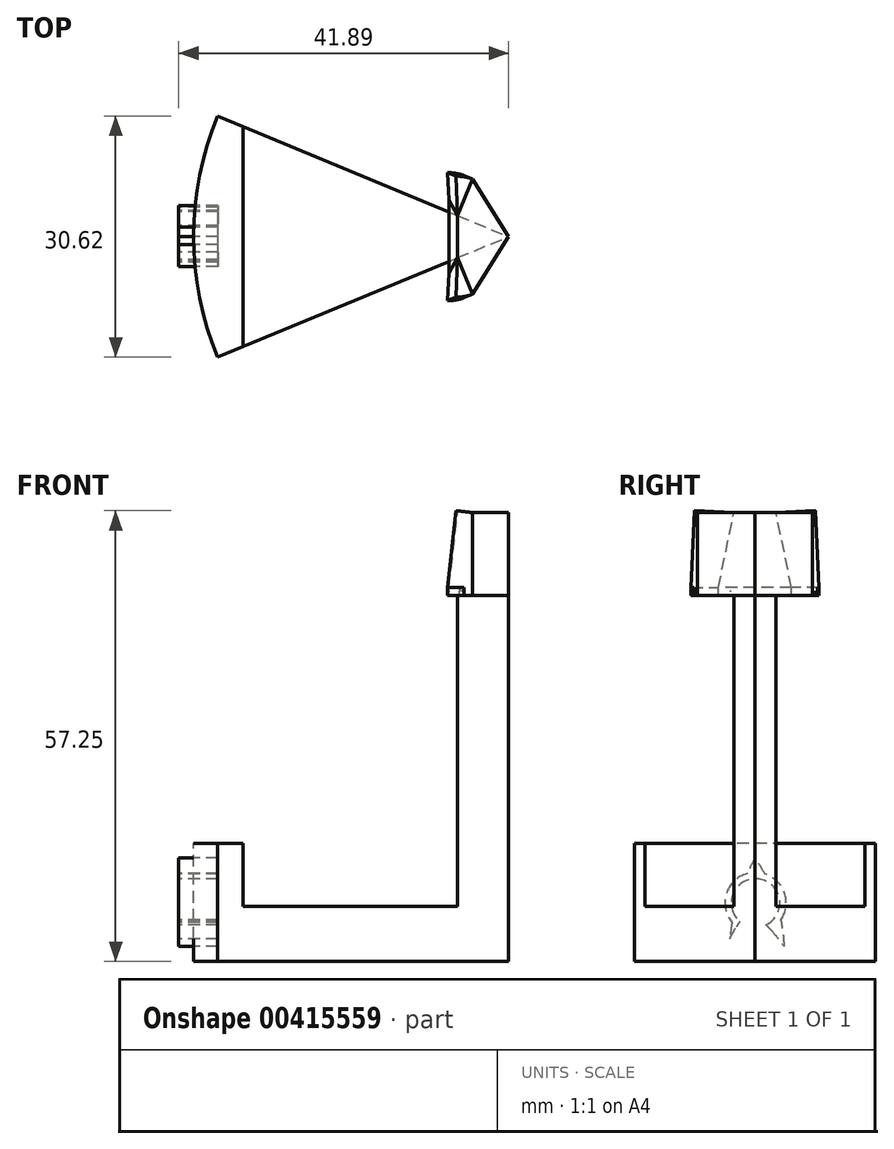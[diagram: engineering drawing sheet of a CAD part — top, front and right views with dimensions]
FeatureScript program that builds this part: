
annotation { "Feature Type Name" : "Feature", "Feature Type Description" : "" }
export const myFeature = defineFeature(function(context is Context, id is Id, definition is map)
    precondition{}
    {
        {
            var Q0;
            Q0=qCreatedBy(makeId("Front.planeOp"),FACE);
            var sketch = newSketch(context, id + "F0", { "sketchPlane" : qUnion([Q0])});
            skLineSegment(sketch, "E0", {"start": v(-37.1, 26.7) * mm, "end": v(-30.1, 26.7) * mm});
            skLineSegment(sketch, "E1", {"start": v(-30.1, 26.7) * mm, "end": v(-30.1, -30.3) * mm});
            skLineSegment(sketch, "E2", {"start": v(-30.1, -30.3) * mm, "end": v(-70.1, -30.3) * mm});
            skLineSegment(sketch, "E3", {"start": v(-70.1, -30.3) * mm, "end": v(-70.1, -15.3) * mm});
            skLineSegment(sketch, "E4", {"start": v(-70.1, -15.3) * mm, "end": v(-63.1, -15.3) * mm});
            skLineSegment(sketch, "E5", {"start": v(-63.1, -15.3) * mm, "end": v(-63.1, -23.3) * mm});
            skLineSegment(sketch, "E6", {"start": v(-63.1, -23.3) * mm, "end": v(-43.1, -23.3) * mm});
            skLineSegment(sketch, "E7", {"start": v(-37.1, 26.7) * mm, "end": v(-43.1, -23.3) * mm});
            skSolve(sketch);
        }
        {
            var Q0;
            Q0=makeQuery(id+"F0.imprint","IMPRINT",FACE,{"disambiguationData":[TD([[makeQuery(id+"F0.imprint","IMPRINT",EDGE,{"derivedFrom":sQuery(id+"F0.wireOp",EDGE,"E0")}),-1.0]])]});
            var Q1;
            Q1=sQuery(id+"F0.wireOp",EDGE,"E1");
            revolve(context, id + "F1", {"entities" : qUnion([Q0]), "axis" : qUnion([Q1]), "revolveType" : RevolveType.SYMMETRIC, "angle" : 45 * degree});
        }
        {
            var Q0;
            Q0=makeQuery(id+"F1.opRevolve","CAP_FACE",FACE,{"disambiguationData":[OSD([sQuery(id+"F0.wireOp",EDGE,"E0"),sQuery(id+"F0.wireOp",EDGE,"E1"),sQuery(id+"F0.wireOp",EDGE,"E2"),sQuery(id+"F0.wireOp",EDGE,"E3"),sQuery(id+"F0.wireOp",EDGE,"E4"),sQuery(id+"F0.wireOp",EDGE,"E5"),sQuery(id+"F0.wireOp",EDGE,"E6"),sQuery(id+"F0.wireOp",EDGE,"E7")])],"isStart":true});
            var sketch = newSketch(context, id + "F2", { "sketchPlane" : qUnion([Q0])});
            skLineSegment(sketch, "E8", {"start": v(-34.81, 26.7) * mm, "end": v(-27.81, 26.7) * mm});
            skLineSegment(sketch, "E9", {"start": v(-27.81, 26.7) * mm, "end": v(-27.81, 16.7) * mm});
            skLineSegment(sketch, "E10", {"start": v(-27.81, 16.7) * mm, "end": v(-36.01, 16.7) * mm});
            skLineSegment(sketch, "E11", {"start": v(-36.01, 16.7) * mm, "end": v(-34.81, 26.7) * mm});
            skSolve(sketch);
        }
        {
            var Q0;
            Q0 = qSketchRegion(id + "F2", true);
            extrude(context, id + "F3", {"entities" : qUnion([Q0]), "operationType" : NewBodyOperationType.ADD, "depth" : 5 * mm});
        }
        {
            var Q0;
            Q0=makeQuery(id+"F1.opRevolve","CAP_FACE",FACE,{"disambiguationData":[OSD([sQuery(id+"F0.wireOp",EDGE,"E0"),sQuery(id+"F0.wireOp",EDGE,"E1"),sQuery(id+"F0.wireOp",EDGE,"E2"),sQuery(id+"F0.wireOp",EDGE,"E3"),sQuery(id+"F0.wireOp",EDGE,"E4"),sQuery(id+"F0.wireOp",EDGE,"E5"),sQuery(id+"F0.wireOp",EDGE,"E6"),sQuery(id+"F0.wireOp",EDGE,"E7")])],"isStart":false});
            var sketch = newSketch(context, id + "F4", { "sketchPlane" : qUnion([Q0])});
            skLineSegment(sketch, "E12", {"start": v(27.81, 26.7) * mm, "end": v(27.81, 16.7) * mm});
            skLineSegment(sketch, "E13", {"start": v(27.81, 16.7) * mm, "end": v(36.01, 16.7) * mm});
            skLineSegment(sketch, "E14", {"start": v(36.01, 16.7) * mm, "end": v(34.81, 26.7) * mm});
            skLineSegment(sketch, "E15", {"start": v(34.81, 26.7) * mm, "end": v(27.81, 26.7) * mm});
            skSolve(sketch);
        }
        {
            var Q0;
            Q0 = qSketchRegion(id + "F4", true);
            extrude(context, id + "F5", {"entities" : qUnion([Q0]), "operationType" : NewBodyOperationType.ADD, "depth" : 5 * mm});
        }
        {
            var Q0;
            Q0=makeQuery(id+"F5.boolean.opBoolean","MERGE",FACE,{"derivedFrom":[makeQuery(id+"F3.boolean.opBoolean","MERGE",FACE,{"derivedFrom":[makeQuery(id+"F1.opRevolve","SWEPT_FACE",FACE,{"disambiguationData":[OSD([sQuery(id+"F0.wireOp",EDGE,"E0")])]}),makeQuery(id+"F3.opExtrude","SWEPT_FACE",FACE,{"disambiguationData":[OSD([sQuery(id+"F2.wireOp",EDGE,"E8")])]})]}),makeQuery(id+"F5.opExtrude","SWEPT_FACE",FACE,{"disambiguationData":[OSD([sQuery(id+"F4.wireOp",EDGE,"E15")])]})]});
            var sketch = newSketch(context, id + "F6", { "sketchPlane" : qUnion([Q0])});
            skLineSegment(sketch, "E16.0", {"start": v(-34.66, 7.3) * mm, "end": v(-36.57, 2.68) * mm});
            skArc(sketch, "E16.1", {"start": v(-36.57, 2.68) * mm, "mid": v(-37.1, 0) * mm, "end": v(-36.57, -2.68) * mm});
            skLineSegment(sketch, "E16.2", {"start": v(-34.66, -7.3) * mm, "end": v(-36.57, -2.68) * mm});
            skLineSegment(sketch, "E17", {"start": v(-34.66, 7.3) * mm, "end": v(-30.1, 0) * mm});
            skLineSegment(sketch, "E18", {"start": v(-30.1, 0) * mm, "end": v(-34.66, -7.3) * mm});
            skLineSegment(sketch, "E19", {"start": v(-36.57, -2.68) * mm, "end": v(-36.57, -7.3) * mm});
            skLineSegment(sketch, "E20", {"start": v(-36.57, -7.3) * mm, "end": v(-34.66, -7.3) * mm});
            skLineSegment(sketch, "E21", {"start": v(-36.57, 2.68) * mm, "end": v(-36.57, 7.3) * mm});
            skLineSegment(sketch, "E22", {"start": v(-36.57, 7.3) * mm, "end": v(-34.66, 7.3) * mm});
            skSolve(sketch);
        }
        {
            var Q0;
            Q0=makeQuery(id+"F6.imprint","IMPRINT",FACE,{"disambiguationData":[TD([[makeQuery(id+"F6.imprint","IMPRINT",EDGE,{"derivedFrom":sQuery(id+"F6.wireOp",EDGE,"E17")}),1.0]])]});
            var Q1;
            Q1=makeQuery(id+"F6.imprint","IMPRINT",FACE,{"disambiguationData":[TD([[makeQuery(id+"F6.imprint","IMPRINT",EDGE,{"derivedFrom":sQuery(id+"F6.wireOp",EDGE,"E18")}),1.0]])]});
            extrude(context, id + "F7", {"entities" : qUnion([Q0, Q1]), "operationType" : NewBodyOperationType.REMOVE, "oppositeDirection" : true, "depth" : 25 * mm});
        }
        {
            var Q0;
            Q0=makeQuery(id+"F5.opExtrude","SWEPT_FACE",FACE,{"disambiguationData":[OSD([sQuery(id+"F4.wireOp",EDGE,"E14")])]});
            var Q1;
            Q1=makeQuery(id+"F5.boolean.opBoolean","MERGE",EDGE,{"derivedFrom":[makeQuery(id+"F1.opRevolve","CAP_EDGE",EDGE,{"disambiguationData":[OSD([sQuery(id+"F0.wireOp",EDGE,"E7")])],"isStart":false}),makeQuery(id+"F5.opExtrude","CAP_EDGE",EDGE,{"disambiguationData":[OSD([sQuery(id+"F4.wireOp",EDGE,"E14")])],"isStart":true})]});
            revolve(context, id + "F8", {"operationType" : NewBodyOperationType.ADD, "entities" : qUnion([Q0]), "axis" : qUnion([Q1]), "revolveType" : RevolveType.ONE_DIRECTION, "oppositeDirection" : true, "angle" : 25 * degree});
        }
        {
            var Q0;
            Q0=makeQuery(id+"F3.opExtrude","SWEPT_FACE",FACE,{"disambiguationData":[OSD([sQuery(id+"F2.wireOp",EDGE,"E11")])]});
            var Q1;
            Q1=makeQuery(id+"F3.boolean.opBoolean","MERGE",EDGE,{"derivedFrom":[makeQuery(id+"F1.opRevolve","CAP_EDGE",EDGE,{"disambiguationData":[OSD([sQuery(id+"F0.wireOp",EDGE,"E7")])],"isStart":true}),makeQuery(id+"F3.opExtrude","CAP_EDGE",EDGE,{"disambiguationData":[OSD([sQuery(id+"F2.wireOp",EDGE,"E11")])],"isStart":true})]});
            revolve(context, id + "F9", {"operationType" : NewBodyOperationType.ADD, "entities" : qUnion([Q0]), "axis" : qUnion([Q1]), "revolveType" : RevolveType.ONE_DIRECTION, "angle" : 25 * degree});
        }
        {
            var Q0;
            Q0=makeQuery(id+"F5.boolean.opBoolean","MERGE",FACE,{"derivedFrom":[makeQuery(id+"F3.boolean.opBoolean","MERGE",FACE,{"derivedFrom":[makeQuery(id+"F1.opRevolve","SWEPT_FACE",FACE,{"disambiguationData":[OSD([sQuery(id+"F0.wireOp",EDGE,"E0")])]}),makeQuery(id+"F3.opExtrude","SWEPT_FACE",FACE,{"disambiguationData":[OSD([sQuery(id+"F2.wireOp",EDGE,"E8")])]})]}),makeQuery(id+"F5.opExtrude","SWEPT_FACE",FACE,{"disambiguationData":[OSD([sQuery(id+"F4.wireOp",EDGE,"E15")])]})]});
            var sketch = newSketch(context, id + "F10", { "sketchPlane" : qUnion([Q0])});
            skPoint(sketch, "E23.0", {"position": v(-36.57, 2.68) * mm});
            skPoint(sketch, "E23.1", {"position": v(-36.57, -2.68) * mm});
            skLineSegment(sketch, "E24", {"start": v(-36.57, 2.68) * mm, "end": v(-36.57, -2.68) * mm});
            skArc(sketch, "E25.0", {"start": v(-36.57, 2.68) * mm, "mid": v(-37.1, 0) * mm, "end": v(-36.57, -2.68) * mm});
            skArc(sketch, "E26.0", {"start": v(-42.12, 4.97) * mm, "mid": v(-43.1, 0) * mm, "end": v(-42.12, -4.97) * mm});
            skLineSegment(sketch, "E27.0", {"start": v(-37.68, 3.14) * mm, "end": v(-42.12, 4.97) * mm});
            skLineSegment(sketch, "E27.1", {"start": v(-37.68, -3.14) * mm, "end": v(-42.12, -4.97) * mm});
            skLineSegment(sketch, "E27.2", {"start": v(-36.57, -2.68) * mm, "end": v(-37.68, -3.14) * mm});
            skLineSegment(sketch, "E27.3", {"start": v(-36.57, 2.68) * mm, "end": v(-37.68, 3.14) * mm});
            skSolve(sketch);
        }
        {
            var Q0;
            Q0=makeQuery(id+"F10.imprint","IMPRINT",FACE,{"disambiguationData":[TD([[makeQuery(id+"F10.imprint","IMPRINT",EDGE,{"derivedFrom":sQuery(id+"F10.wireOp",EDGE,"E25.0")}),-1.0]])]});
            var Q1;
            Q1=makeQuery(id+"F10.imprint","IMPRINT",FACE,{"disambiguationData":[TD([[makeQuery(id+"F10.imprint","IMPRINT",EDGE,{"derivedFrom":sQuery(id+"F10.wireOp",EDGE,"E24")}),-1.0]])]});
            var Q2;
            Q2=makeQuery(id+"F1.opRevolve","SWEPT_FACE",FACE,{"disambiguationData":[OSD([sQuery(id+"F0.wireOp",EDGE,"E6")])]});
            extrude(context, id + "F11", {"entities" : qUnion([Q0, Q1]), "operationType" : NewBodyOperationType.REMOVE, "endBound" : BoundingType.UP_TO_SURFACE, "oppositeDirection" : true, "endBoundEntityFace" : qUnion([Q2]), "depth" : 25 * mm});
        }
        {
            var Q0;
            Q0=makeQuery(id+"F11.boolean.opBoolean","COPY",FACE,{"derivedFrom":makeQuery(id+"F11.opExtrude","SWEPT_FACE",FACE,{"disambiguationData":[OSD([sQuery(id+"F10.wireOp",EDGE,"E24")])]})});
            var sketch = newSketch(context, id + "F12", { "sketchPlane" : qUnion([Q0])});
            skLineSegment(sketch, "E28", {"start": v(-2.68, 16.7) * mm, "end": v(-2.68, 26.7) * mm});
            skLineSegment(sketch, "E29", {"start": v(-2.68, 26.7) * mm, "end": v(2.68, 26.7) * mm});
            skLineSegment(sketch, "E30", {"start": v(2.68, 26.7) * mm, "end": v(2.68, 16.7) * mm});
            skLineSegment(sketch, "E31", {"start": v(2.68, 16.7) * mm, "end": v(-2.68, 16.7) * mm});
            skSolve(sketch);
        }
        {
            var Q0;
            Q0 = qSketchRegion(id + "F12", true);
            var Q1;
            Q1=sQuery(id+"F12.wireOp",EDGE,"E29");
            revolve(context, id + "F13", {"operationType" : NewBodyOperationType.ADD, "entities" : qUnion([Q0]), "axis" : qUnion([Q1]), "revolveType" : RevolveType.ONE_DIRECTION, "oppositeDirection" : true, "angle" : 6.75 * degree});
        }
        {
            var Q0;
            Q0=makeQuery(id+"F13.opRevolve","SWEPT_FACE",FACE,{"disambiguationData":[OSD([sQuery(id+"F12.wireOp",EDGE,"E28")])]});
            var Q1;
            Q1=makeQuery(id+"F13.opRevolve","SWEPT_FACE",FACE,{"disambiguationData":[OSD([sQuery(id+"F12.wireOp",EDGE,"E30")])]});
            extrude(context, id + "F14", {"entities" : qUnion([Q0, Q1]), "operationType" : NewBodyOperationType.ADD, "depth" : 2 * mm, "hasSecondDirection" : true, "secondDirectionOppositeDirection" : true, "secondDirectionDepth" : 2 * mm});
        }
        {
            var Q0;
            Q0=makeQuery(id+"F11.boolean.opBoolean","COPY",FACE,{"derivedFrom":makeQuery(id+"F11.opExtrude","SWEPT_FACE",FACE,{"disambiguationData":[OSD([sQuery(id+"F10.wireOp",EDGE,"E27.0"),sQuery(id+"F10.wireOp",EDGE,"E27.3")])]})});
            var Q1;
            {var subQ2=sQuery(id+"F4.wireOp",EDGE,"E14");var subQ3=sQuery(id+"F4.wireOp",EDGE,"E13");Q1=makeQuery(id+"F14.boolean.opBoolean","SPLIT",FACE,{"disambiguationData":[TD([makeQuery(id+"F5.opExtrude","SWEPT_FACE",FACE,{"disambiguationData":[OSD([subQ3])]})])],"derivedFrom":makeQuery(id+"F8.opRevolve","CAP_FACE",FACE,{"disambiguationData":[OSD([subQ2])],"isStart":false})});}
            extrude(context, id + "F15", {"entities" : qUnion([Q0, Q1]), "operationType" : NewBodyOperationType.REMOVE, "oppositeDirection" : true, "depth" : 25 * mm});
        }
        {
            var Q0;
            Q0=makeQuery(id+"F5.opExtrude","SWEPT_FACE",FACE,{"disambiguationData":[OSD([sQuery(id+"F4.wireOp",EDGE,"E13")])]});
            var sketch = newSketch(context, id + "F16", { "sketchPlane" : qUnion([Q0])});
            skLineSegment(sketch, "E32.2", {"start": v(-37.89, -8.13) * mm, "end": v(-37.75, -4.81) * mm});
            skEllipticalArc(sketch, "E32.3", {});
            skFitSpline(sketch, "E32.4", {"points": [v(-36.3, -7.94) * mm, v(-36.12, -7.9) * mm, v(-35.94, -7.83) * mm, v(-35.76, -7.75) * mm]});
            skLineSegment(sketch, "E32.5", {"start": v(-35.76, -7.75) * mm, "end": v(-34.66, -7.3) * mm});
            skLineSegment(sketch, "E32.7", {"start": v(-37.75, -3.17) * mm, "end": v(-37.75, -4.68) * mm});
            skLineSegment(sketch, "E33", {"start": v(-37.67, -3.14) * mm, "end": v(-37.68, -3.14) * mm});
            skPoint(sketch, "E34.orphan", {"position": v(-37.75, 4.68) * mm});
            skLineSegment(sketch, "E35", {"start": v(-37.75, -4.68) * mm, "end": v(-37.75, -4.81) * mm});
            skPoint(sketch, "E36.orphan", {"position": v(-37.74, -4.68) * mm});
            skLineSegment(sketch, "E37.0", {"start": v(-37.75, 4.68) * mm, "end": v(-37.75, -4.68) * mm});
            skLineSegment(sketch, "E37.1", {"start": v(-36.57, 2.68) * mm, "end": v(-36.57, -2.68) * mm});
            skLineSegment(sketch, "E38.0", {"start": v(-37.89, 8.13) * mm, "end": v(-37.75, 4.78) * mm});
            skEllipticalArc(sketch, "E38.1", {});
            skLineSegment(sketch, "E38.2", {"start": v(-34.66, 7.3) * mm, "end": v(-35.77, 7.76) * mm});
            skLineSegment(sketch, "E38.3", {"start": v(-34.66, 7.3) * mm, "end": v(-30.1, 0) * mm});
            skLineSegment(sketch, "E39", {"start": v(-37.75, 4.68) * mm, "end": v(-37.75, 4.78) * mm});
            skPoint(sketch, "E40.orphan", {"position": v(-37.74, 4.68) * mm});
            skLineSegment(sketch, "E41.0", {"start": v(-30.1, 0) * mm, "end": v(-36.57, 2.68) * mm});
            skLineSegment(sketch, "E42", {"start": v(-34.66, -7.3) * mm, "end": v(-30.1, 0) * mm});
            skLineSegment(sketch, "E43", {"start": v(-36.57, -2.68) * mm, "end": v(-30.1, 0) * mm});
            const initialGuessF16  = {"E32.3": [-0.0376813648399324, -0.003138004145393734, -0.3826834323650902, 0.9238795325112866, 0.005, 0.004964384192434613, 2.7052603405912126, 3.0272844520744475], "E38.1": [-0.0376813648399324, 0.0031380041453937433, -0.3826834323650934, -0.9238795325112852, 0.005, 0.004964384192434612, 3.1415926535897927, 3.577924966588377]};
            skSetInitialGuess(sketch, initialGuessF16);
            skSolve(sketch);
        }
        {
            var Q0;
            Q0 = qSketchRegion(id + "F16", true);
            extrude(context, id + "F17", {"entities" : qUnion([Q0]), "operationType" : NewBodyOperationType.ADD, "depth" : .5 * mm});
        }
        {
            var Q0;
            Q0=makeQuery(id+"F17.opExtrude","CAP_FACE",FACE,{"disambiguationData":[OSD([sQuery(id+"F16.wireOp",EDGE,"E32.2"),sQuery(id+"F16.wireOp",EDGE,"E32.3"),sQuery(id+"F16.wireOp",EDGE,"E32.4"),sQuery(id+"F16.wireOp",EDGE,"E32.5"),sQuery(id+"F16.wireOp",EDGE,"E35"),sQuery(id+"F16.wireOp",EDGE,"E37.0"),sQuery(id+"F16.wireOp",EDGE,"E38.0"),sQuery(id+"F16.wireOp",EDGE,"E38.1"),sQuery(id+"F16.wireOp",EDGE,"E38.2"),sQuery(id+"F16.wireOp",EDGE,"E38.3"),sQuery(id+"F16.wireOp",EDGE,"E39"),sQuery(id+"F16.wireOp",EDGE,"E42")])],"isStart":true});
            extrude(context, id + "F18", {"entities" : qUnion([Q0]), "operationType" : NewBodyOperationType.ADD, "depth" : .5 * mm});
        }
        {
            var Q0;
            Q0=makeQuery(id+"F18.opExtrude","CAP_FACE",FACE,{"disambiguationData":[OSD([sQuery(id+"F16.wireOp",EDGE,"E32.2"),sQuery(id+"F16.wireOp",EDGE,"E32.3"),sQuery(id+"F16.wireOp",EDGE,"E32.4"),sQuery(id+"F16.wireOp",EDGE,"E32.5"),sQuery(id+"F16.wireOp",EDGE,"E35"),sQuery(id+"F16.wireOp",EDGE,"E37.0"),sQuery(id+"F16.wireOp",EDGE,"E38.0"),sQuery(id+"F16.wireOp",EDGE,"E38.1"),sQuery(id+"F16.wireOp",EDGE,"E38.2"),sQuery(id+"F16.wireOp",EDGE,"E38.3"),sQuery(id+"F16.wireOp",EDGE,"E39"),sQuery(id+"F16.wireOp",EDGE,"E42")])],"isStart":false});
            var Q1;
            Q1=makeQuery(id+"F17.opExtrude","CAP_FACE",FACE,{"disambiguationData":[OSD([sQuery(id+"F16.wireOp",EDGE,"E32.2"),sQuery(id+"F16.wireOp",EDGE,"E32.3"),sQuery(id+"F16.wireOp",EDGE,"E32.4"),sQuery(id+"F16.wireOp",EDGE,"E32.5"),sQuery(id+"F16.wireOp",EDGE,"E35"),sQuery(id+"F16.wireOp",EDGE,"E37.0"),sQuery(id+"F16.wireOp",EDGE,"E38.0"),sQuery(id+"F16.wireOp",EDGE,"E38.1"),sQuery(id+"F16.wireOp",EDGE,"E38.2"),sQuery(id+"F16.wireOp",EDGE,"E38.3"),sQuery(id+"F16.wireOp",EDGE,"E39"),sQuery(id+"F16.wireOp",EDGE,"E42")])],"isStart":false});
            extrude(context, id + "F19", {"entities" : qUnion([Q0]), "operationType" : NewBodyOperationType.REMOVE, "endBound" : BoundingType.UP_TO_SURFACE, "oppositeDirection" : true, "endBoundEntityFace" : qUnion([Q1]), "depth" : 25 * mm});
        }
        {
            var Q0;
            Q0=makeQuery(id+"F1.opRevolve","SWEPT_FACE",FACE,{"disambiguationData":[OSD([sQuery(id+"F0.wireOp",EDGE,"E4")])]});
            var sketch = newSketch(context, id + "F20", { "sketchPlane" : qUnion([Q0])});
            skArc(sketch, "E44.0", {"start": v(-60.6, 12.63) * mm, "mid": v(-63.1, 0) * mm, "end": v(-60.6, -12.63) * mm});
            skLineSegment(sketch, "E44.1", {"start": v(-63.83, 13.97) * mm, "end": v(-60.6, 12.63) * mm});
            skLineSegment(sketch, "E44.2", {"start": v(-63.83, -13.97) * mm, "end": v(-60.6, -12.63) * mm});
            skLineSegment(sketch, "E45", {"start": v(-63.83, 13.97) * mm, "end": v(-63.83, -13.97) * mm});
            skPoint(sketch, "E46.orphan", {"position": v(-67.06, -15.3) * mm});
            skPoint(sketch, "E47.orphan", {"position": v(-67.06, 15.3) * mm});
            skSolve(sketch);
        }
        {
            var Q0;
            Q0 = qSketchRegion(id + "F20", true);
            var Q1;
            {var subQ0=sQuery(id+"F0.wireOp",EDGE,"E6");Q1=makeQuery(id+"F11.boolean.opBoolean","MERGE",FACE,{"derivedFrom":[makeQuery(id+"F1.opRevolve","SWEPT_FACE",FACE,{"disambiguationData":[OSD([subQ0])]}),makeQuery(id+"F11.opExtrude","CAP_FACE",FACE,{"disambiguationData":[OSD([subQ0])],"isStart":false})]});}
            extrude(context, id + "F21", {"entities" : qUnion([Q0]), "operationType" : NewBodyOperationType.REMOVE, "endBound" : BoundingType.UP_TO_SURFACE, "oppositeDirection" : true, "endBoundEntityFace" : qUnion([Q1]), "depth" : 25 * mm});
        }
        {
            var Q0;
            Q0=qCreatedBy(makeId("Right.planeOp"),FACE);
            cPlane(context, id + "F22", {"entities" : qUnion([Q0]), "cplaneType" : CPlaneType.OFFSET, "offset" : 72 * mm, "oppositeDirection" : true, "width" : 150 * mm, "height" : 150 * mm});
        }
        {
            var Q0;
            Q0=qCreatedBy(id+"F22.planeOp",FACE);
            var sketch = newSketch(context, id + "F23", { "sketchPlane" : qUnion([Q0])});
            skPoint(sketch, "E48.0", {"position": v(-15.3, -22.8) * mm});
            skPoint(sketch, "E48.1", {"position": v(15.3, -22.8) * mm});
            skArc(sketch, "E49", {"start": v(-1.18, -19.19) * mm, "mid": v(-3.66, -21.6) * mm, "end": v(-3.26, -25.02) * mm});
            skArc(sketch, "E50", {"start": v(3.27, -27.45) * mm, "mid": v(3.15, -26.41) * mm, "end": v(3, -25.38) * mm});
            skArc(sketch, "E51", {"start": v(0.04, -17.16) * mm, "mid": v(-0.6, -18.16) * mm, "end": v(-1.18, -19.19) * mm});
            skFitSpline(sketch, "E52", {"points": [v(3.27, -27.45) * mm, v(1.97, -25.2) * mm, v(1.39, -24.54) * mm, v(1.06, -24.3) * mm, v(0.85, -24.33) * mm, v(0.05, -24.64) * mm, v(-1.02, -25.4) * mm, v(-2.02, -26.39) * mm, v(-3.67, -28.4) * mm], "startDerivative": vector(-4.37, 10.3) * mm, "endDerivative": vector(-9.31, -11.35) * mm});
            skArc(sketch, "E53.trimOffspring", {"start": v(-1.92, -26.28) * mm, "mid": v(0.32, -26.77) * mm, "end": v(2.45, -25.92) * mm});
            skArc(sketch, "E54.trimOffspring", {"start": v(3, -25.38) * mm, "mid": v(3.71, -21.74) * mm, "end": v(1.06, -19.15) * mm});
            skArc(sketch, "E55.trimOffspring", {"start": v(-1.35, -19.53) * mm, "mid": v(-2.42, -22.03) * mm, "end": v(-3.18, -24.65) * mm});
            skArc(sketch, "E56.trimOffspring", {"start": v(1.06, -19.15) * mm, "mid": v(0.57, -18.14) * mm, "end": v(0.04, -17.16) * mm});
            skArc(sketch, "E57.trimOffspring", {"start": v(-3.26, -25.02) * mm, "mid": v(-3.53, -26.7) * mm, "end": v(-3.67, -28.4) * mm});
            skArc(sketch, "E58.trimOffspring", {"start": v(2.93, -25.03) * mm, "mid": v(2.22, -22.2) * mm, "end": v(1.2, -19.47) * mm});
            skArc(sketch, "E59.0", {"start": v(2.38, -24.87) * mm, "mid": v(2.95, -21.98) * mm, "end": v(0.84, -19.92) * mm});
            skArc(sketch, "E60.0", {"start": v(-0.94, -19.95) * mm, "mid": v(-2.9, -21.86) * mm, "end": v(-2.59, -24.58) * mm});
            skCircle(sketch, "E61", {"center": v(0, -22.9) * mm, "radius": 3.09 * mm});
            skSolve(sketch);
        }
        {
            var Q0;
            {var subQ0=sQuery(id+"F23.wireOp",EDGE,"E61");var subQ1=makeQuery(id+"F23.imprint","IMPRINT",VERTEX,{"disambiguationData":[OD(0.0)],"derivedFrom":subQ0});Q0=makeQuery(id+"F23.imprint","IMPRINT",FACE,{"disambiguationData":[TD([[makeQuery(id+"F23.imprint","IMPRINT",EDGE,{"disambiguationData":[TD([[subQ1,-1.0]])],"derivedFrom":subQ0}),1.0]])]});}
            var Q1;
            Q1=makeQuery(id+"F23.imprint","IMPRINT",FACE,{"disambiguationData":[TD([[makeQuery(id+"F23.imprint","IMPRINT",EDGE,{"derivedFrom":sQuery(id+"F23.wireOp",EDGE,"E49")}),1.0]])]});
            extrude(context, id + "F24", {"entities" : qUnion([Q0, Q1]), "oppositeDirection" : true, "depth" : 5 * mm});
        }
        {
            var Q0;
            Q0=makeQuery(id+"F24.opExtrude","CAP_FACE",FACE,{"disambiguationData":[OSD([sQuery(id+"F23.wireOp",EDGE,"E49"),sQuery(id+"F23.wireOp",EDGE,"E50"),sQuery(id+"F23.wireOp",EDGE,"E51"),sQuery(id+"F23.wireOp",EDGE,"E52"),sQuery(id+"F23.wireOp",EDGE,"E53.trimOffspring"),sQuery(id+"F23.wireOp",EDGE,"E54.trimOffspring"),sQuery(id+"F23.wireOp",EDGE,"E55.trimOffspring"),sQuery(id+"F23.wireOp",EDGE,"E56.trimOffspring"),sQuery(id+"F23.wireOp",EDGE,"E57.trimOffspring"),sQuery(id+"F23.wireOp",EDGE,"E52"),sQuery(id+"F23.wireOp",EDGE,"E52"),sQuery(id+"F23.wireOp",EDGE,"E58.trimOffspring"),sQuery(id+"F23.wireOp",EDGE,"E61")])],"isStart":false});
            var sketch = newSketch(context, id + "F25", { "sketchPlane" : qUnion([Q0])});
            skLineSegment(sketch, "E62", {"start": v(-0.04, -17.16) * mm, "end": v(-0.04, -26.78) * mm, "construction": true});
            skSolve(sketch);
        }
        {
            var Q0;
            Q0=makeQuery(id+"F24.opExtrude","SWEPT_BODY",BODY,{"disambiguationData":[OSD([sQuery(id+"F23.wireOp",EDGE,"E49"),sQuery(id+"F23.wireOp",EDGE,"E50"),sQuery(id+"F23.wireOp",EDGE,"E51"),sQuery(id+"F23.wireOp",EDGE,"E52"),sQuery(id+"F23.wireOp",EDGE,"E53.trimOffspring"),sQuery(id+"F23.wireOp",EDGE,"E54.trimOffspring"),sQuery(id+"F23.wireOp",EDGE,"E55.trimOffspring"),sQuery(id+"F23.wireOp",EDGE,"E56.trimOffspring"),sQuery(id+"F23.wireOp",EDGE,"E57.trimOffspring"),sQuery(id+"F23.wireOp",EDGE,"E52"),sQuery(id+"F23.wireOp",EDGE,"E52"),sQuery(id+"F23.wireOp",EDGE,"E58.trimOffspring"),sQuery(id+"F23.wireOp",EDGE,"E61")])]});
            var Q1;
            Q1=sQuery(id+"F25.wireOp",EDGE,"E62");
            transform(context, id + "F26", {"entities" : qUnion([Q0]), "transformType" : TransformType.ROTATION, "transformAxis" : qUnion([Q1]), "angle" : 180 * degree, "makeCopy" : false});
        }
        {
            var Q0;
            Q0=makeQuery(id+"F24.opExtrude","SWEPT_BODY",BODY,{"disambiguationData":[OSD([sQuery(id+"F23.wireOp",EDGE,"E49"),sQuery(id+"F23.wireOp",EDGE,"E50"),sQuery(id+"F23.wireOp",EDGE,"E51"),sQuery(id+"F23.wireOp",EDGE,"E52"),sQuery(id+"F23.wireOp",EDGE,"E53.trimOffspring"),sQuery(id+"F23.wireOp",EDGE,"E54.trimOffspring"),sQuery(id+"F23.wireOp",EDGE,"E55.trimOffspring"),sQuery(id+"F23.wireOp",EDGE,"E56.trimOffspring"),sQuery(id+"F23.wireOp",EDGE,"E57.trimOffspring"),sQuery(id+"F23.wireOp",EDGE,"E52"),sQuery(id+"F23.wireOp",EDGE,"E52"),sQuery(id+"F23.wireOp",EDGE,"E58.trimOffspring"),sQuery(id+"F23.wireOp",EDGE,"E61")])]});
            var Q1;
            Q1=makeQuery(id+"F21.boolean.opBoolean","COPY",FACE,{"derivedFrom":makeQuery(id+"F21.opExtrude","SWEPT_FACE",FACE,{"disambiguationData":[OSD([sQuery(id+"F20.wireOp",EDGE,"E45")])]})});
            transform(context, id + "F27", {"entities" : qUnion([Q0]), "transformType" : TransformType.TRANSLATION_DISTANCE, "transformDirection" : qUnion([Q1]), "distance" : 10 * mm, "makeCopy" : false});
        }
    });
